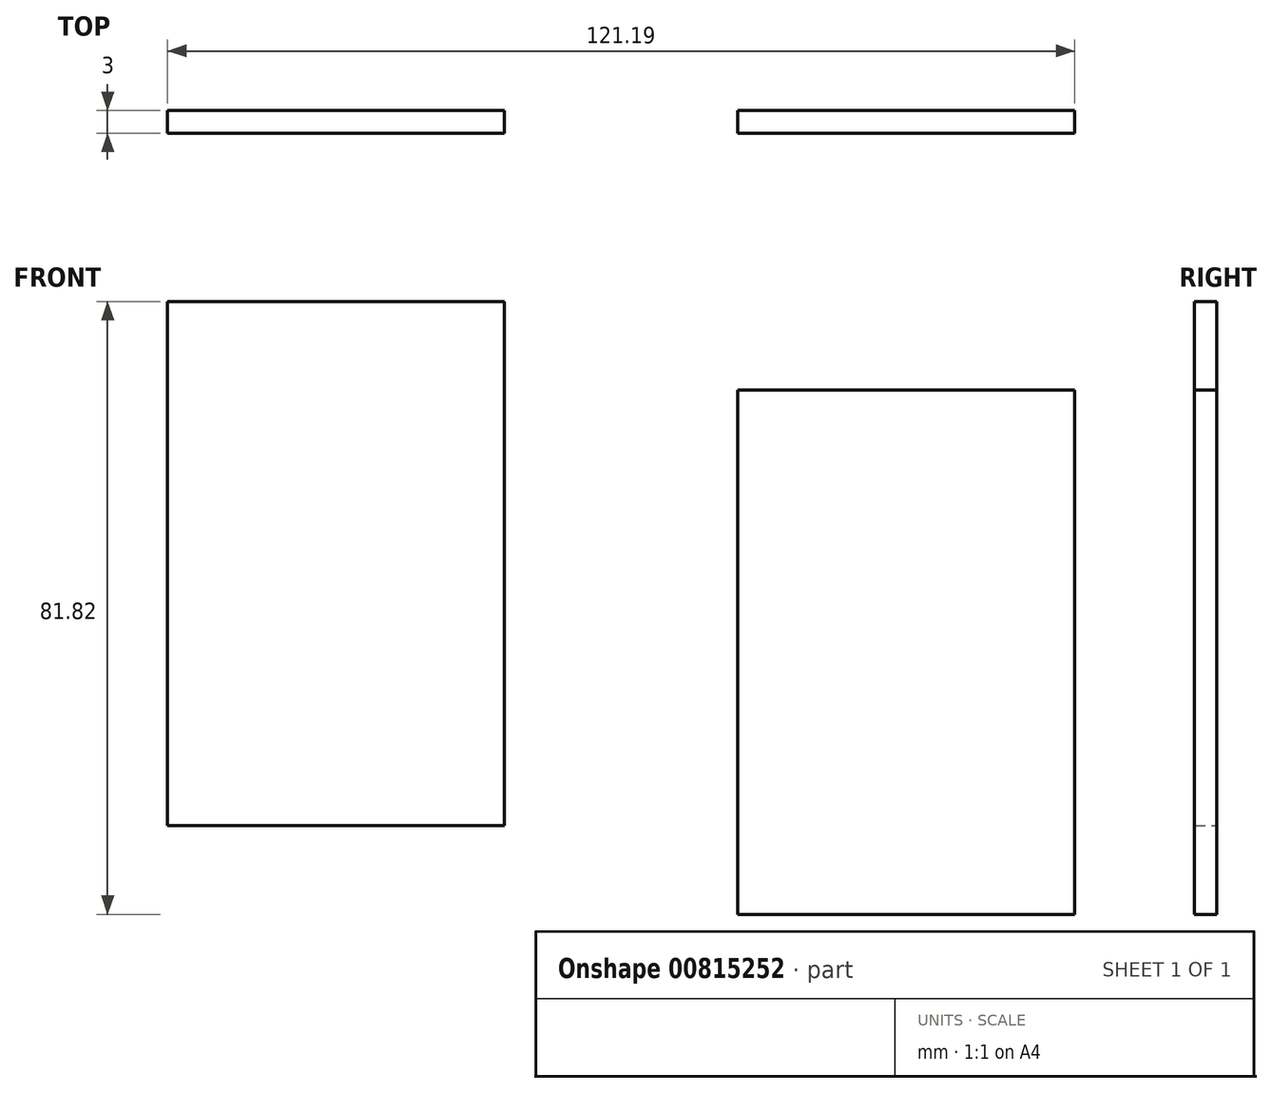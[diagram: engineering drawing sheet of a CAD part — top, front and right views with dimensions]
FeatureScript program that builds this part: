
annotation { "Feature Type Name" : "Feature", "Feature Type Description" : "" }
export const myFeature = defineFeature(function(context is Context, id is Id, definition is map)
    precondition{}
    {
        {
            var Q0;
            Q0=qCreatedBy(makeId("Front.planeOp"),FACE);
            var sketch = newSketch(context, id + "F0", { "sketchPlane" : qUnion([Q0])});
            skLineSegment(sketch, "E0.bottom", {"start": v(-67.98, 42.1) * mm, "end": v(-22.98, 42.1) * mm});
            skLineSegment(sketch, "E0.top", {"start": v(-67.98, -27.9) * mm, "end": v(-22.98, -27.9) * mm});
            skLineSegment(sketch, "E0.left", {"start": v(-67.98, 42.1) * mm, "end": v(-67.98, -27.9) * mm});
            skLineSegment(sketch, "E0.right", {"start": v(-22.98, 42.1) * mm, "end": v(-22.98, -27.9) * mm});
            skLineSegment(sketch, "E1.bottom", {"start": v(8.21, 30.28) * mm, "end": v(53.21, 30.28) * mm});
            skLineSegment(sketch, "E1.top", {"start": v(8.21, -39.72) * mm, "end": v(53.21, -39.72) * mm});
            skLineSegment(sketch, "E1.left", {"start": v(8.21, 30.28) * mm, "end": v(8.21, -39.72) * mm});
            skLineSegment(sketch, "E1.right", {"start": v(53.21, 30.28) * mm, "end": v(53.21, -39.72) * mm});
            skSolve(sketch);
        }
        {
            var Q0;
            Q0=makeQuery(id+"F0.imprint","IMPRINT",FACE,{"disambiguationData":[TD([[makeQuery(id+"F0.imprint","IMPRINT",EDGE,{"derivedFrom":sQuery(id+"F0.wireOp",EDGE,"E0.bottom")}),-1.0]])]});
            var Q1;
            Q1=makeQuery(id+"F0.imprint","IMPRINT",FACE,{"disambiguationData":[TD([[makeQuery(id+"F0.imprint","IMPRINT",EDGE,{"derivedFrom":sQuery(id+"F0.wireOp",EDGE,"E1.bottom")}),-1.0]])]});
            extrude(context, id + "F1", {"entities" : qUnion([Q0, Q1]), "depth" : 3 * mm, "offsetDistance" : 25 * mm});
        }
    });
